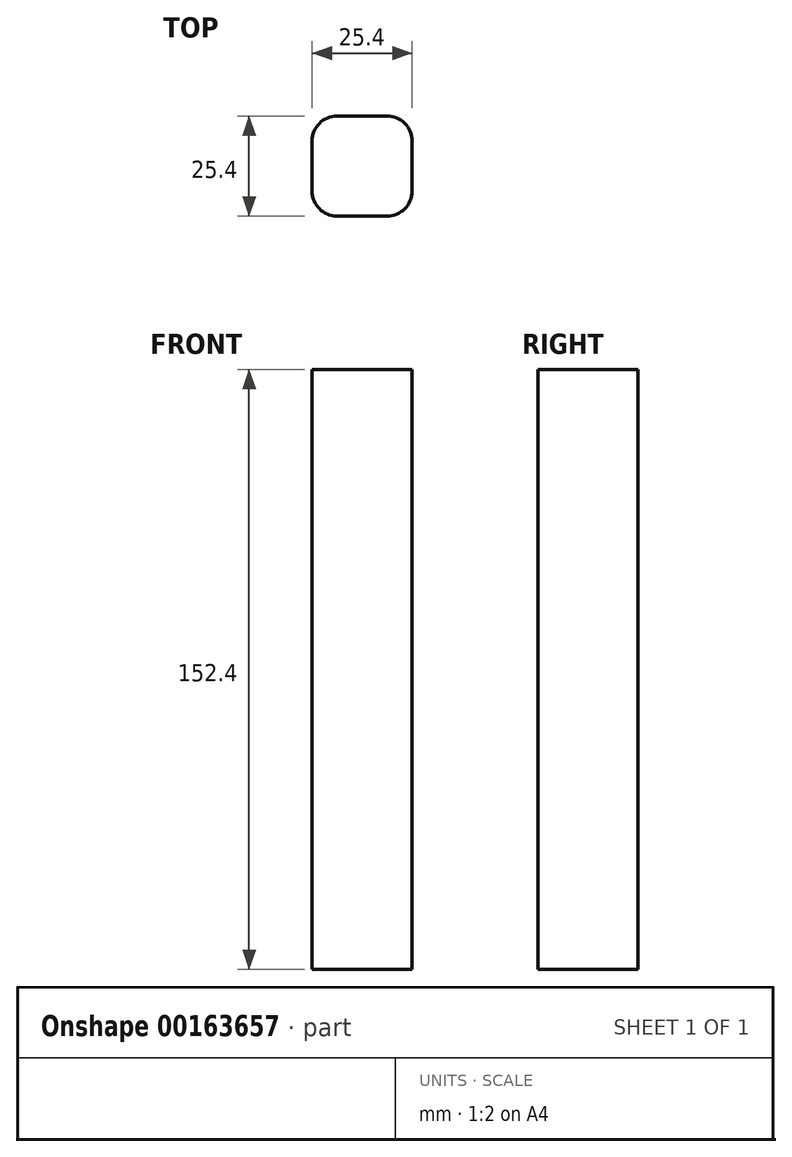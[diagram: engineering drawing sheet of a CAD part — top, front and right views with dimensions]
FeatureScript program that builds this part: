
annotation { "Feature Type Name" : "Feature", "Feature Type Description" : "" }
export const myFeature = defineFeature(function(context is Context, id is Id, definition is map)
    precondition{}
    {
        {
            var Q0;
            Q0=qCreatedBy(makeId("Top.planeOp"),FACE);
            var sketch = newSketch(context, id + "F0", { "sketchPlane" : qUnion([Q0])});
            skLineSegment(sketch, "E0.bottom", {"start": v(6.35, 12.7) * mm, "end": v(-6.35, 12.7) * mm});
            skLineSegment(sketch, "E0.top", {"start": v(6.35, -12.7) * mm, "end": v(-6.35, -12.7) * mm});
            skLineSegment(sketch, "E0.left", {"start": v(12.7, 6.35) * mm, "end": v(12.7, -6.35) * mm});
            skLineSegment(sketch, "E0.right", {"start": v(-12.7, 6.35) * mm, "end": v(-12.7, -6.35) * mm});
            skPoint(sketch, "E0.middle", {"position": v(0, 0) * mm});
            skPoint(sketch, "E1.visualSharp", {"position": v(-12.7, 12.7) * mm});
            skArc(sketch, "E1.filletArc", {"start": v(-6.35, 12.7) * mm, "mid": v(-10.84, 10.84) * mm, "end": v(-12.7, 6.35) * mm});
            skPoint(sketch, "E2.visualSharp", {"position": v(-12.7, -12.7) * mm});
            skArc(sketch, "E2.filletArc", {"start": v(-12.7, -6.35) * mm, "mid": v(-10.84, -10.84) * mm, "end": v(-6.35, -12.7) * mm});
            skPoint(sketch, "E3.visualSharp", {"position": v(12.7, -12.7) * mm});
            skArc(sketch, "E3.filletArc", {"start": v(6.35, -12.7) * mm, "mid": v(10.84, -10.84) * mm, "end": v(12.7, -6.35) * mm});
            skPoint(sketch, "E4.visualSharp", {"position": v(12.7, 12.7) * mm});
            skArc(sketch, "E4.filletArc", {"start": v(12.7, 6.35) * mm, "mid": v(10.84, 10.84) * mm, "end": v(6.35, 12.7) * mm});
            skSolve(sketch);
        }
        {
            var Q0;
            Q0=qSketchRegion(id+"F0",true);
            extrude(context, id + "F1", {"entities" : qUnion([Q0]), "depth" : 152.4 * mm, "offsetDistance" : 25.4 * mm});
        }
    });
